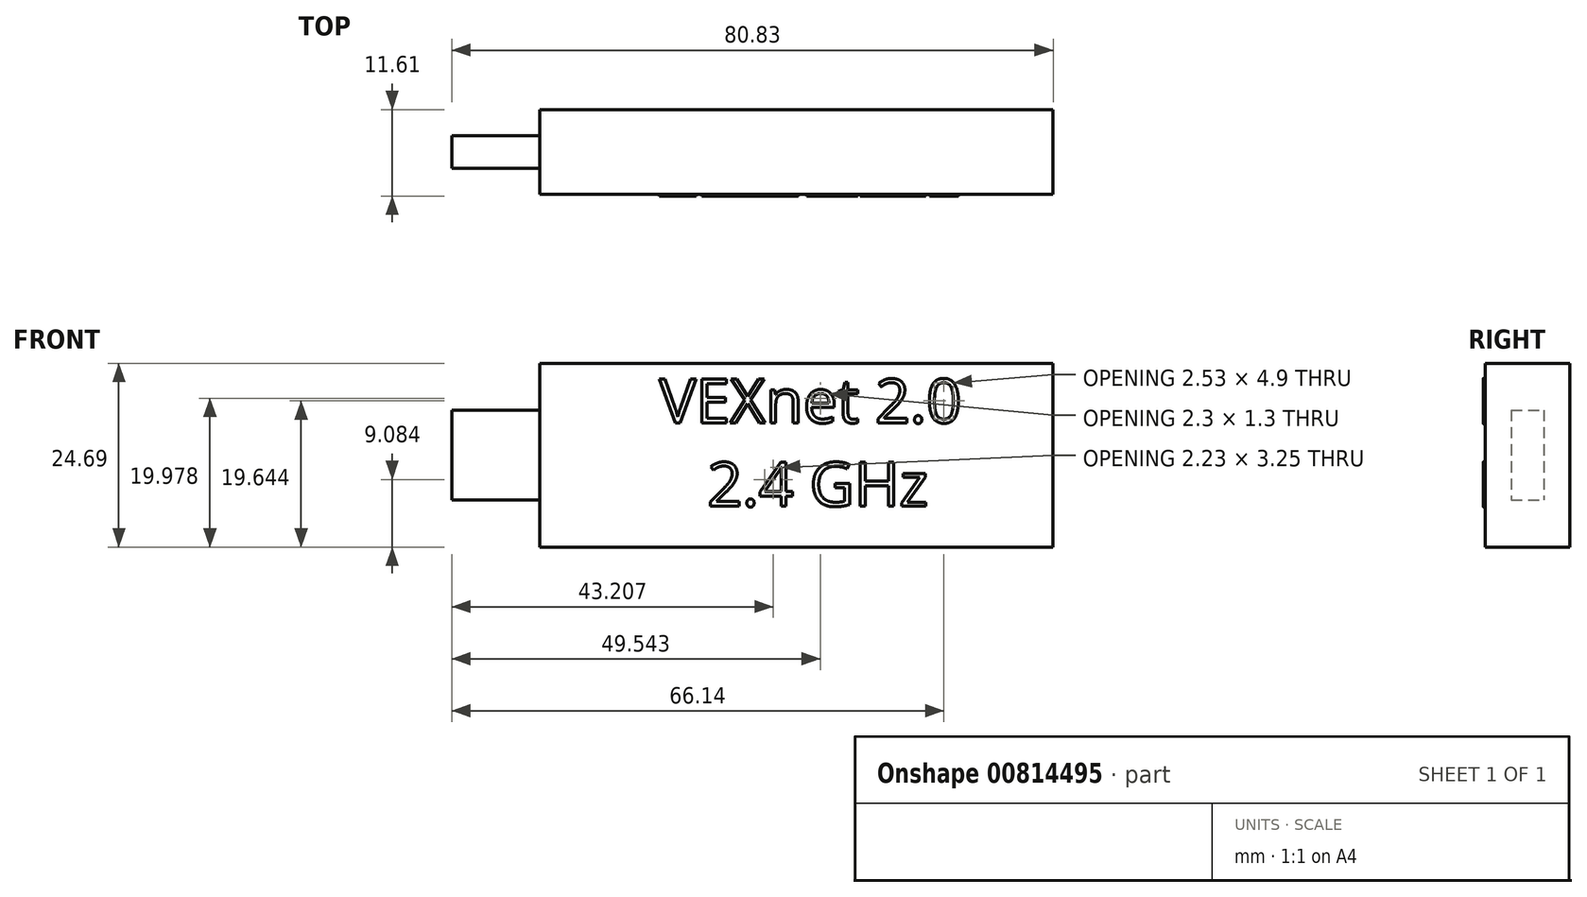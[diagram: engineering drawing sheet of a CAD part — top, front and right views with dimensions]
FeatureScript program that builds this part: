
annotation { "Feature Type Name" : "Feature", "Feature Type Description" : "" }
export const myFeature = defineFeature(function(context is Context, id is Id, definition is map)
    precondition{}
    {
        {
            var Q0;
            Q0=qCreatedBy(makeId("Front.planeOp"),FACE);
            var sketch = newSketch(context, id + "F0", { "sketchPlane" : qUnion([Q0])});
            skLineSegment(sketch, "E0.bottom", {"start": v(-42.01, 12.26) * mm, "end": v(27, 12.26) * mm});
            skLineSegment(sketch, "E0.top", {"start": v(-42.01, -12.43) * mm, "end": v(27, -12.43) * mm});
            skLineSegment(sketch, "E0.left", {"start": v(-42.01, 12.26) * mm, "end": v(-42.01, -12.43) * mm});
            skLineSegment(sketch, "E0.right", {"start": v(27, 12.26) * mm, "end": v(27, -12.43) * mm});
            skLineSegment(sketch, "E1.bottom", {"start": v(-42.01, 5.99) * mm, "end": v(-53.83, 5.99) * mm});
            skLineSegment(sketch, "E1.top", {"start": v(-42.01, -6.13) * mm, "end": v(-53.83, -6.13) * mm});
            skLineSegment(sketch, "E1.left", {"start": v(-42.01, 5.99) * mm, "end": v(-42.01, -6.13) * mm});
            skLineSegment(sketch, "E1.right", {"start": v(-53.83, 5.99) * mm, "end": v(-53.83, -6.13) * mm});
            skSolve(sketch);
        }
        {
            var Q0;
            {var subQ3=sQuery(id+"F0.wireOp",EDGE,"E0.bottom");Q0=makeQuery(id+"F0.imprint","IMPRINT",FACE,{"disambiguationData":[TD([[makeQuery(id+"F0.imprint","IMPRINT",EDGE,{"derivedFrom":subQ3}),-1.0]])]});}
            extrude(context, id + "F1", {"entities" : qUnion([Q0]), "endBound" : BoundingType.SYMMETRIC, "depth" : 11.35 * mm, "offsetDistance" : 25.4 * mm});
        }
        {
            var Q0;
            Q0=makeQuery(id+"F0.imprint","IMPRINT",FACE,{"disambiguationData":[TD([[makeQuery(id+"F0.imprint","IMPRINT",EDGE,{"derivedFrom":sQuery(id+"F0.wireOp",EDGE,"E1.bottom")}),1.0]])]});
            extrude(context, id + "F2", {"entities" : qUnion([Q0]), "operationType" : NewBodyOperationType.ADD, "endBound" : BoundingType.SYMMETRIC, "depth" : 4.4 * mm, "offsetDistance" : 25.4 * mm});
        }
        {
            var Q0;
            Q0=makeQuery(id+"F1.opExtrude","CAP_FACE",FACE,{"disambiguationData":[OSD([sQuery(id+"F0.wireOp",EDGE,"E0.bottom"),sQuery(id+"F0.wireOp",EDGE,"E0.top"),sQuery(id+"F0.wireOp",EDGE,"E0.left"),sQuery(id+"F0.wireOp",EDGE,"E0.right"),sQuery(id+"F0.wireOp",EDGE,"E1.left")])],"isStart":false});
            var sketch = newSketch(context, id + "F3", { "sketchPlane" : qUnion([Q0])});
            skText(sketch, "E2", { "text": "VEXnet 2.0\n   2.4 GHz", "fontName": "OpenSans-Regular.ttf"});
            const initialGuessF3  = {"E2": [-0.0259, 0.00427, 1, 0, 0.00593]};
            skSetInitialGuess(sketch, initialGuessF3);
            skSolve(sketch);
        }
        {
            var Q0;
            Q0 = qSketchRegion(id + "F3", true);
            extrude(context, id + "F4", {"entities" : qUnion([Q0]), "depth" : 0.25 * mm, "offsetDistance" : 25.4 * mm});
        }
    });
